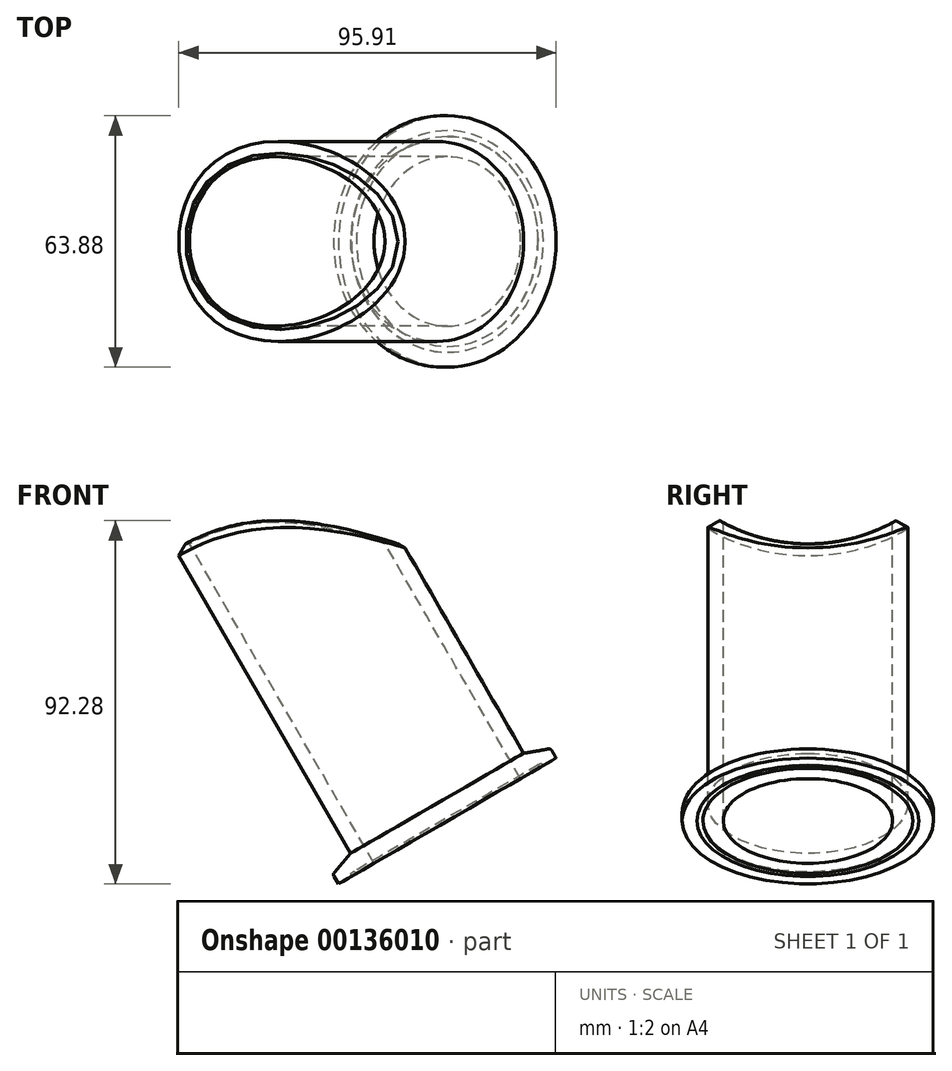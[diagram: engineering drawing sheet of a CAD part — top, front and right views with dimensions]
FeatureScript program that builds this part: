
annotation { "Feature Type Name" : "Feature", "Feature Type Description" : "" }
export const myFeature = defineFeature(function(context is Context, id is Id, definition is map)
    precondition{}
    {
        {
            var Q0;
            Q0=qCreatedBy(makeId("Front.planeOp"),FACE);
            var sketch = newSketch(context, id + "F0", { "sketchPlane" : qUnion([Q0])});
            skLineSegment(sketch, "E0", {"start": v(0, 0) * mm, "end": v(32.14, 18.55) * mm, "construction": true});
            skLineSegment(sketch, "E1", {"start": v(15, -25.98) * mm, "end": v(81.55, 12.44) * mm, "construction": true});
            skLineSegment(sketch, "E2", {"start": v(0, 0) * mm, "end": v(34.84, -60.35) * mm, "construction": true});
            skLineSegment(sketch, "E3", {"start": v(39.25, -11.98) * mm, "end": v(63.15, -53.37) * mm, "construction": true});
            skLineSegment(sketch, "E4", {"start": v(57.87, -1.23) * mm, "end": v(117.87, -105.15) * mm});
            skLineSegment(sketch, "E5", {"start": v(117.87, -105.15) * mm, "end": v(122.35, -102.57) * mm});
            skLineSegment(sketch, "E6", {"start": v(126.9, -99.93) * mm, "end": v(125.79, -98) * mm});
            skLineSegment(sketch, "E7", {"start": v(124.96, -97.6) * mm, "end": v(118.66, -98.72) * mm});
            skLineSegment(sketch, "E8", {"start": v(118.66, -98.72) * mm, "end": v(61.25, 0.72) * mm});
            skLineSegment(sketch, "E9", {"start": v(61.25, 0.72) * mm, "end": v(57.87, -1.23) * mm});
            skPoint(sketch, "E10.visualSharp", {"position": v(125.5, -97.5) * mm});
            skArc(sketch, "E10.filletArc", {"start": v(125.79, -98) * mm, "mid": v(125.43, -97.67) * mm, "end": v(124.96, -97.6) * mm});
            skArc(sketch, "E11", {"start": v(123.64, -101.82) * mm, "mid": v(122.62, -101.54) * mm, "end": v(122.35, -102.57) * mm});
            skLineSegment(sketch, "E12.trimOffspring", {"start": v(123.64, -101.82) * mm, "end": v(126.9, -99.93) * mm});
            skLineSegment(sketch, "E13", {"start": v(0, 0) * mm, "end": v(-29.37, 0) * mm, "construction": true});
            skSolve(sketch);
        }
        {
            var Q0;
            Q0 = qSketchRegion(id + "F0", true);
            var Q1;
            Q1=sQuery(id+"F0.wireOp",EDGE,"E3");
            revolve(context, id + "F1", {"entities" : qUnion([Q0]), "axis" : qUnion([Q1]), "revolveType" : RevolveType.FULL});
        }
        {
            var Q0;
            Q0=qCreatedBy(makeId("Right.planeOp"),FACE);
            var sketch = newSketch(context, id + "F2", { "sketchPlane" : qUnion([Q0])});
            skCircle(sketch, "E14", {"center": v(0, 0) * mm, "radius": 45.5 * mm});
            skSolve(sketch);
        }
        {
            var Q0;
            Q0 = qSketchRegion(id + "F2", true);
            extrude(context, id + "F3", {"entities" : qUnion([Q0]), "operationType" : NewBodyOperationType.REMOVE, "depth" : 113 * mm});
        }
        {
            var Q0;
            Q0=makeQuery(id+"F3.boolean.opBoolean","INTERSECT",EDGE,{"derivedFrom":[makeQuery(id+"F1.opRevolve","SWEPT_FACE",FACE,{"disambiguationData":[OSD([sQuery(id+"F0.wireOp",EDGE,"E8")])]}),makeQuery(id+"F3.opExtrude","SWEPT_FACE",FACE,{"disambiguationData":[OSD([sQuery(id+"F2.wireOp",EDGE,"E14")])]})]});
            chamfer(context, id + "F4", {"entities" : qUnion([Q0]), "width" : 2 * mm, "tangentPropagation" : true});
        }
    });
